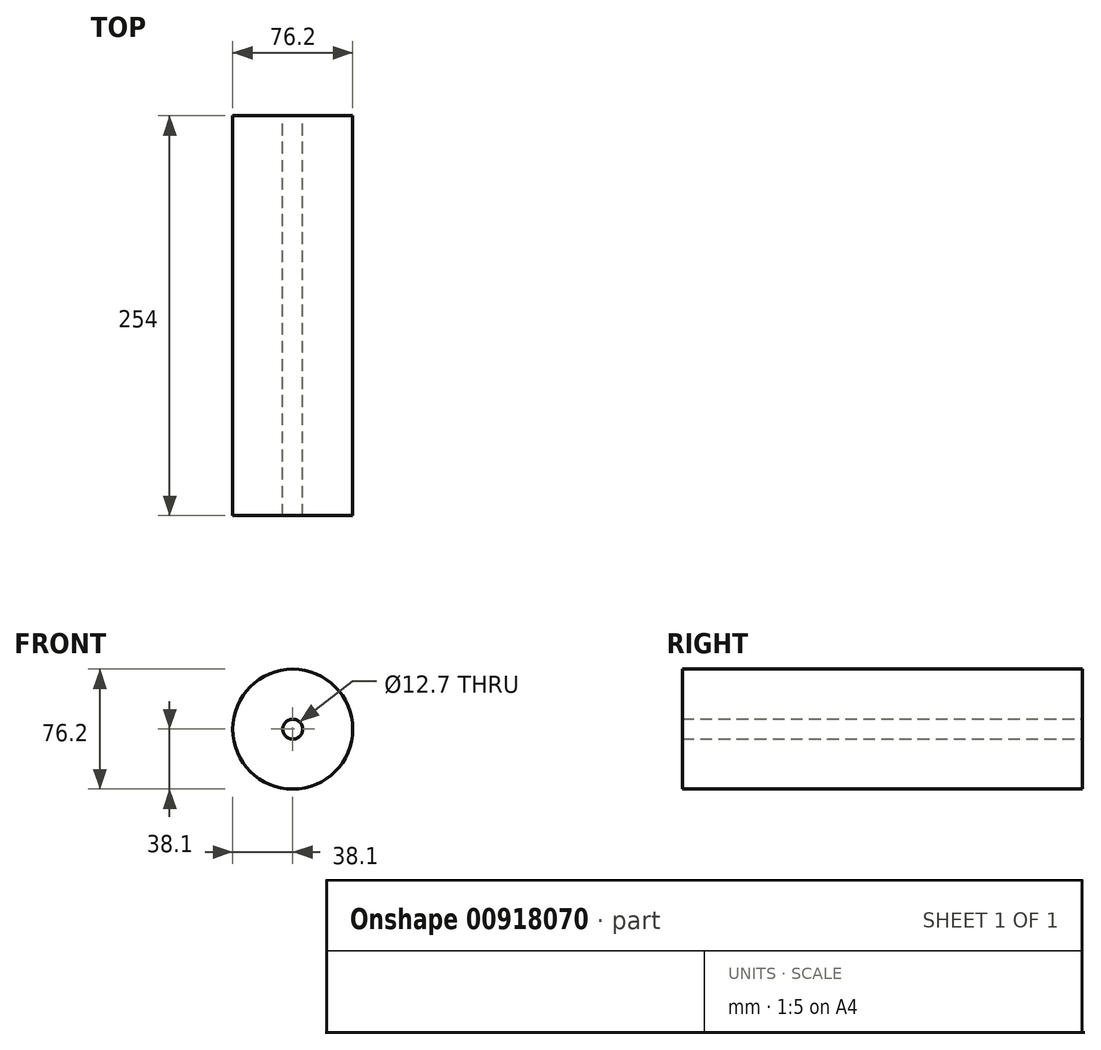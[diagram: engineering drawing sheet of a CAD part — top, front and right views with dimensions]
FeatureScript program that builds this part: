
annotation { "Feature Type Name" : "Feature", "Feature Type Description" : "" }
export const myFeature = defineFeature(function(context is Context, id is Id, definition is map)
    precondition{}
    {
        {
            var Q0;
            Q0=qCreatedBy(makeId("Front.planeOp"),FACE);
            var sketch = newSketch(context, id + "F0", { "sketchPlane" : qUnion([Q0])});
            skCircle(sketch, "E0", {"center": v(0, 0) * mm, "radius": 38.1 * mm});
            skCircle(sketch, "E1", {"center": v(0, 0) * mm, "radius": 6.35 * mm});
            skSolve(sketch);
        }
        {
            var Q0;
            Q0=makeQuery(id+"F0.imprint","IMPRINT",FACE,{"disambiguationData":[TD([[makeQuery(id+"F0.imprint","IMPRINT",EDGE,{"derivedFrom":sQuery(id+"F0.wireOp",EDGE,"E0")}),1.0]])]});
            extrude(context, id + "F1", {"entities" : qUnion([Q0]), "depth" : 254 * mm, "offsetDistance" : 25.4 * mm});
        }
    });
